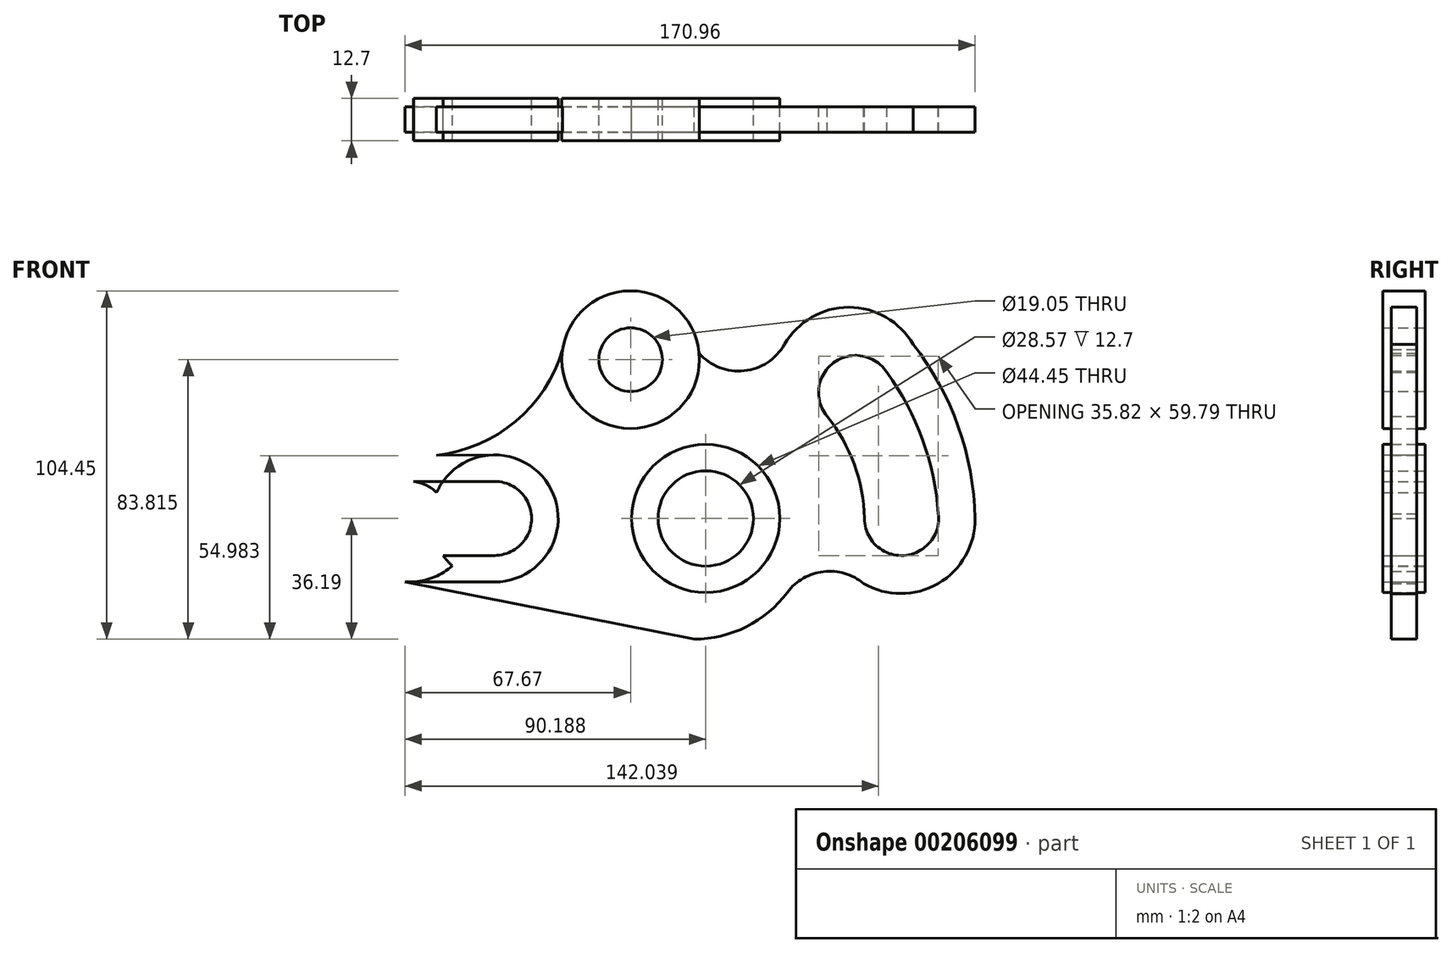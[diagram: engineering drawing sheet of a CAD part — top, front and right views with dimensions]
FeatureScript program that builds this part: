
annotation { "Feature Type Name" : "Feature", "Feature Type Description" : "" }
export const myFeature = defineFeature(function(context is Context, id is Id, definition is map)
    precondition{}
    {
        {
            var Q0;
            Q0=qCreatedBy(makeId("Front.planeOp"),FACE);
            var sketch = newSketch(context, id + "F0", { "sketchPlane" : qUnion([Q0])});
            skCircle(sketch, "E0", {"center": v(-7.9, 0) * mm, "radius": 14.29 * mm});
            skCircle(sketch, "E1", {"center": v(-30.4, 47.63) * mm, "radius": 9.53 * mm});
            skCircle(sketch, "E2", {"center": v(-96.59, 0) * mm, "radius": 11.1 * mm});
            skCircle(sketch, "E3", {"center": v(-71.19, 0) * mm, "radius": 11.1 * mm});
            skLineSegment(sketch, "E4", {"start": v(-96.59, -11.1) * mm, "end": v(-71.19, -11.1) * mm});
            skCircle(sketch, "E5", {"center": v(-30.4, 47.63) * mm, "radius": 20.64 * mm});
            skCircle(sketch, "E6", {"center": v(-7.9, 0) * mm, "radius": 22.23 * mm});
            skCircle(sketch, "E7", {"center": v(-96.59, 0) * mm, "radius": 19.05 * mm});
            skCircle(sketch, "E8", {"center": v(-71.19, 0) * mm, "radius": 19.05 * mm});
            skLineSegment(sketch, "E9", {"start": v(-98.69, 18.93) * mm, "end": v(-71.27, 19.05) * mm});
            skLineSegment(sketch, "E10", {"start": v(-98.08, -19) * mm, "end": v(-71.23, -19.05) * mm});
            skCircle(sketch, "E11", {"center": v(50.83, 0) * mm, "radius": 11.13 * mm});
            skCircle(sketch, "E12", {"center": v(37.1, 37.75) * mm, "radius": 11.13 * mm});
            skArc(sketch, "E13", {"start": v(39.7, 0) * mm, "mid": v(36.64, 16.2) * mm, "end": v(28.57, 30.6) * mm});
            skArc(sketch, "E14", {"start": v(61.96, 0) * mm, "mid": v(57.12, 23.66) * mm, "end": v(45.62, 44.9) * mm});
            skArc(sketch, "E15", {"start": v(-88.62, 18.98) * mm, "mid": v(-64.9, 29.11) * mm, "end": v(-50.82, 50.71) * mm});
            skArc(sketch, "E16", {"start": v(-9.86, 49.52) * mm, "mid": v(3.63, 44.3) * mm, "end": v(15.75, 52.18) * mm});
            skArc(sketch, "E17", {"start": v(39.45, -19.5) * mm, "mid": v(61.85, -19.5) * mm, "end": v(72.88, 0) * mm});
            skArc(sketch, "E18", {"start": v(72.88, 0) * mm, "mid": v(67.84, 27.6) * mm, "end": v(54.3, 52.18) * mm});
            skArc(sketch, "E19", {"start": v(16.6, -22.2) * mm, "mid": v(4.27, -32.5) * mm, "end": v(-11.36, -36.19) * mm});
            skArc(sketch, "E20", {"start": v(16.6, -22.2) * mm, "mid": v(27.44, -15.95) * mm, "end": v(39.45, -19.5) * mm});
            skArc(sketch, "E21", {"start": v(15.75, 52.18) * mm, "mid": v(35.02, 63.34) * mm, "end": v(54.3, 52.18) * mm});
            skLineSegment(sketch, "E22", {"start": v(-11.36, -36.19) * mm, "end": v(-98.08, -19) * mm});
            skLineSegment(sketch, "E23", {"start": v(-97.62, 11.05) * mm, "end": v(-71.2, 11.1) * mm});
            skSolve(sketch);
        }
        {
            var Q0;
            Q0=makeQuery(id+"F0.imprint","IMPRINT",FACE,{"disambiguationData":[TD([[makeQuery(id+"F0.imprint","IMPRINT",EDGE,{"derivedFrom":sQuery(id+"F0.wireOp",EDGE,"E6")}),-1.0]])]});
            extrude(context, id + "F1", {"entities" : qUnion([Q0]), "endBound" : BoundingType.SYMMETRIC, "depth" : 7.62 * mm});
        }
        {
            var Q0;
            {var subQ5=sQuery(id+"F0.wireOp",EDGE,"E2");var subQ7=sQuery(id+"F0.wireOp",EDGE,"E23");var subQ8=makeQuery(id+"F0.imprint","INTERSECT",VERTEX,{"disambiguationData":[OD(0.0)],"derivedFrom":[subQ5,subQ7]});Q0=makeQuery(id+"F0.imprint","IMPRINT",FACE,{"disambiguationData":[TD([[makeQuery(id+"F0.imprint","IMPRINT",EDGE,{"disambiguationData":[TD([[subQ8,1.0]])],"derivedFrom":subQ5}),-1.0]])]});}
            var Q1;
            {var subQ0=sQuery(id+"F0.wireOp",EDGE,"E9");var subQ1=sQuery(id+"F0.wireOp",EDGE,"E7");var subQ2=makeQuery(id+"F0.imprint","INTERSECT",VERTEX,{"disambiguationData":[OD(1.0)],"derivedFrom":[subQ1,subQ0]});Q1=makeQuery(id+"F0.imprint","IMPRINT",FACE,{"disambiguationData":[TD([[makeQuery(id+"F0.imprint","IMPRINT",EDGE,{"disambiguationData":[TD([[subQ2,1.0]])],"derivedFrom":subQ1}),-1.0]])]});}
            var Q2;
            {var subQ5=sQuery(id+"F0.wireOp",EDGE,"E4");var subQ6=sQuery(id+"F0.wireOp",EDGE,"E3");var subQ7=makeQuery(id+"F0.imprint","INTERSECT",VERTEX,{"derivedFrom":[subQ6,subQ5]});Q2=makeQuery(id+"F0.imprint","IMPRINT",FACE,{"disambiguationData":[TD([[makeQuery(id+"F0.imprint","IMPRINT",EDGE,{"disambiguationData":[TD([[subQ7,-1.0]])],"derivedFrom":subQ6}),-1.0]])]});}
            var Q3;
            {var subQ0=sQuery(id+"F0.wireOp",EDGE,"E10");var subQ1=sQuery(id+"F0.wireOp",EDGE,"E7");var subQ2=makeQuery(id+"F0.imprint","INTERSECT",VERTEX,{"derivedFrom":[subQ1,subQ0]});Q3=makeQuery(id+"F0.imprint","IMPRINT",FACE,{"disambiguationData":[TD([[makeQuery(id+"F0.imprint","IMPRINT",EDGE,{"disambiguationData":[TD([[subQ2,-1.0]])],"derivedFrom":subQ1}),-1.0]])]});}
            var Q4;
            {var subQ0=sQuery(id+"F0.wireOp",EDGE,"E8");var subQ1=sQuery(id+"F0.wireOp",EDGE,"E4");var subQ2=makeQuery(id+"F0.imprint","INTERSECT",VERTEX,{"derivedFrom":[subQ1,subQ0]});Q4=makeQuery(id+"F0.imprint","IMPRINT",FACE,{"disambiguationData":[TD([[makeQuery(id+"F0.imprint","IMPRINT",EDGE,{"disambiguationData":[TD([[subQ2,-1.0]])],"derivedFrom":subQ1}),-1.0]])]});}
            var Q5;
            {var subQ0=sQuery(id+"F0.wireOp",EDGE,"E23");var subQ1=sQuery(id+"F0.wireOp",EDGE,"E7");var subQ2=makeQuery(id+"F0.imprint","INTERSECT",VERTEX,{"derivedFrom":[subQ1,subQ0]});Q5=makeQuery(id+"F0.imprint","IMPRINT",FACE,{"disambiguationData":[TD([[makeQuery(id+"F0.imprint","IMPRINT",EDGE,{"disambiguationData":[TD([[subQ2,-1.0]])],"derivedFrom":subQ1}),1.0]])]});}
            var Q6;
            Q6=makeQuery(id+"F0.imprint","IMPRINT",FACE,{"disambiguationData":[TD([[makeQuery(id+"F0.imprint","IMPRINT",EDGE,{"derivedFrom":sQuery(id+"F0.wireOp",EDGE,"E0")}),-1.0]])]});
            var Q7;
            Q7=makeQuery(id+"F0.imprint","IMPRINT",FACE,{"disambiguationData":[TD([[makeQuery(id+"F0.imprint","IMPRINT",EDGE,{"derivedFrom":sQuery(id+"F0.wireOp",EDGE,"E1")}),-1.0]])]});
            extrude(context, id + "F2", {"entities" : qUnion([Q0, Q1, Q2, Q3, Q4, Q5, Q6, Q7]), "endBound" : BoundingType.SYMMETRIC, "depth" : 12.7 * mm});
        }
    });
